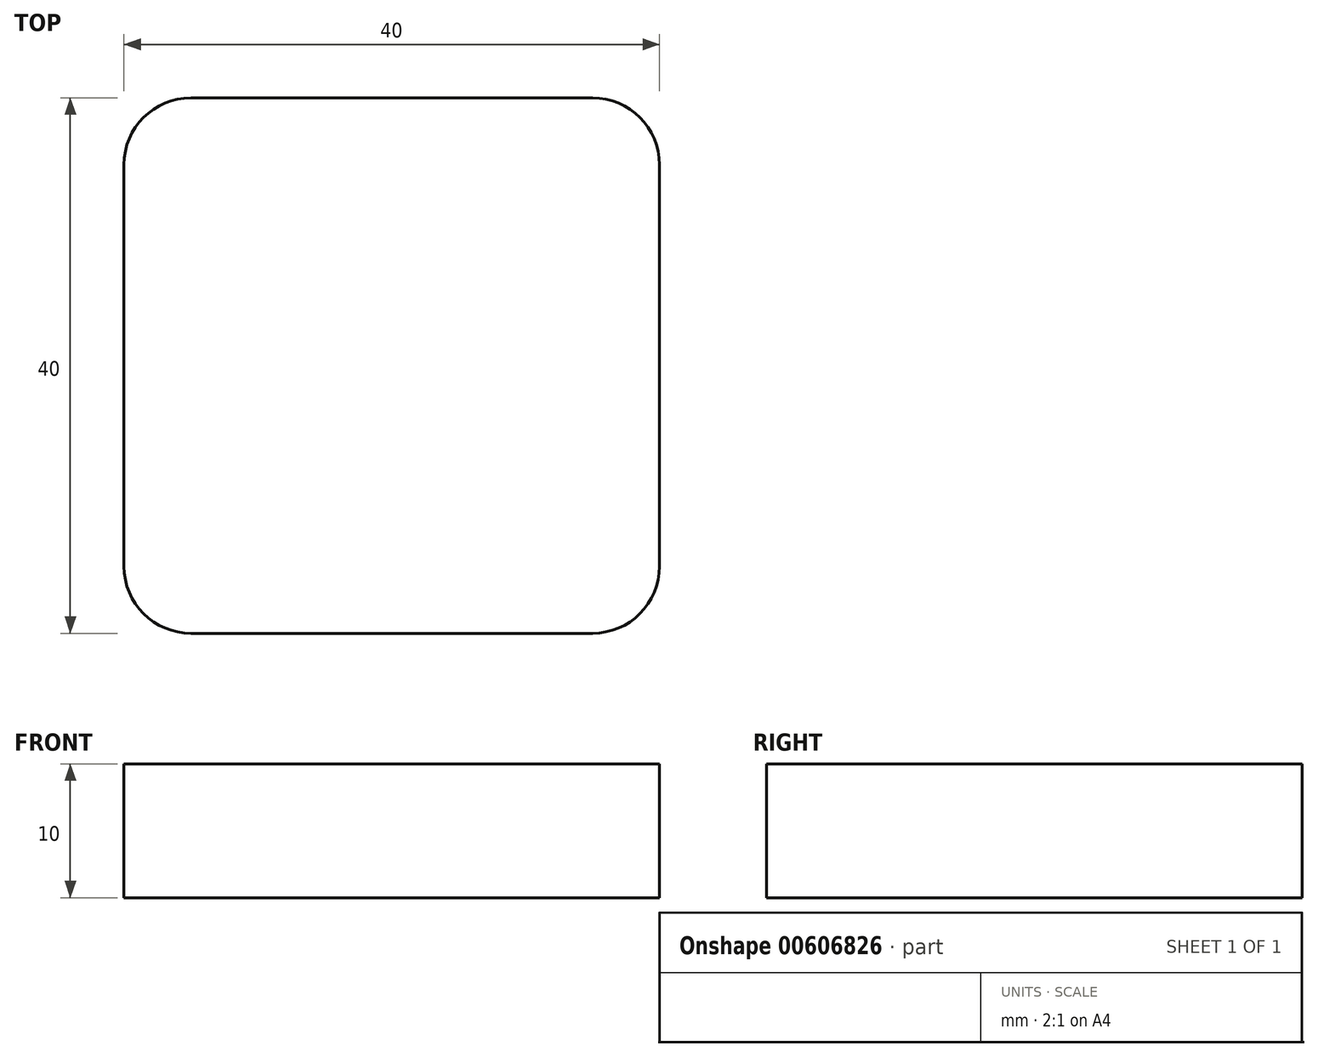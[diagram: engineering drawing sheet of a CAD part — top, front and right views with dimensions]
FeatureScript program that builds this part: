
annotation { "Feature Type Name" : "Feature", "Feature Type Description" : "" }
export const myFeature = defineFeature(function(context is Context, id is Id, definition is map)
    precondition{}
    {
        {
            var Q0;
            Q0=qCreatedBy(makeId("Top.planeOp"),FACE);
            var sketch = newSketch(context, id + "F0", { "sketchPlane" : qUnion([Q0])});
            skLineSegment(sketch, "E0.top", {"start": v(20, -20) * mm, "end": v(-20, -20) * mm});
            skPoint(sketch, "E0.middle", {"position": v(0, 0) * mm});
            skPoint(sketch, "E1", {"position": v(-15, 20) * mm});
            skPoint(sketch, "E2", {"position": v(15, 20) * mm});
            skPoint(sketch, "E3", {"position": v(20, 15) * mm});
            skPoint(sketch, "E4", {"position": v(-20, 15) * mm});
            skLineSegment(sketch, "E5", {"start": v(-15, 20) * mm, "end": v(15, 20) * mm});
            skLineSegment(sketch, "E6", {"start": v(-20, 15) * mm, "end": v(-20, -20) * mm});
            skLineSegment(sketch, "E7", {"start": v(20, -20) * mm, "end": v(20, 15) * mm});
            skLineSegment(sketch, "E8.top", {"start": v(-20, 20) * mm, "end": v(-15, 20) * mm});
            skLineSegment(sketch, "E8.left", {"start": v(-20, 15) * mm, "end": v(-20, 20) * mm});
            skLineSegment(sketch, "E9.bottom", {"start": v(15, 20) * mm, "end": v(20, 20) * mm});
            skLineSegment(sketch, "E9.right", {"start": v(20, 20) * mm, "end": v(20, 15) * mm});
            skSolve(sketch);
        }
        {
            var Q0;
            Q0 = qSketchRegion(id + "F0", true);
            extrude(context, id + "F1", {"entities" : qUnion([Q0]), "depth" : 10 * mm, "offsetDistance" : 25 * mm});
        }
        {
            var Q0;
            Q0=makeQuery(id+"F1.opExtrude","SWEPT_EDGE",EDGE,{"disambiguationData":[OSD([sQuery(id+"F0.wireOp",EDGE,"E8.top"),sQuery(id+"F0.wireOp",EDGE,"E8.left")])]});
            var Q1;
            Q1=makeQuery(id+"F1.opExtrude","SWEPT_EDGE",EDGE,{"disambiguationData":[OSD([sQuery(id+"F0.wireOp",EDGE,"E9.bottom"),sQuery(id+"F0.wireOp",EDGE,"E9.right")])]});
            var Q2;
            Q2=makeQuery(id+"F1.opExtrude","SWEPT_EDGE",EDGE,{"disambiguationData":[OSD([sQuery(id+"F0.wireOp",EDGE,"E0.top"),sQuery(id+"F0.wireOp",EDGE,"E7")])]});
            var Q3;
            Q3=makeQuery(id+"F1.opExtrude","SWEPT_EDGE",EDGE,{"disambiguationData":[OSD([sQuery(id+"F0.wireOp",EDGE,"E0.top"),sQuery(id+"F0.wireOp",EDGE,"E6")])]});
            fillet(context, id + "F2", {"entities" : qUnion([Q0, Q1, Q2, Q3]), "radius" : 5 * mm, "tangentPropagation" : true, "allowEdgeOverflow" : false});
        }
    });
